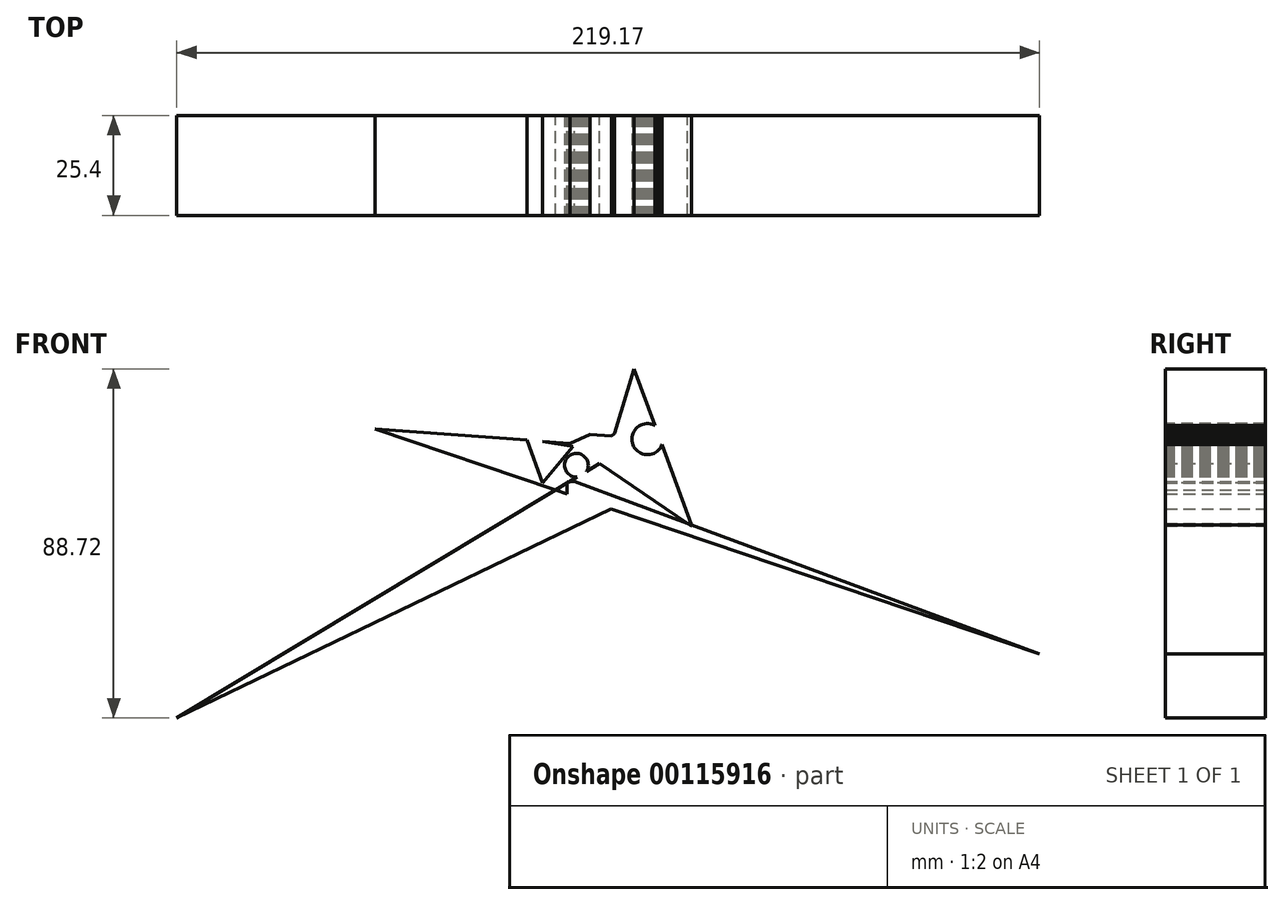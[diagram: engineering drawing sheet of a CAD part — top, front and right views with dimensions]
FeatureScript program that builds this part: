
annotation { "Feature Type Name" : "Feature", "Feature Type Description" : "" }
export const myFeature = defineFeature(function(context is Context, id is Id, definition is map)
    precondition{}
    {
        {
            var Q0;
            Q0=qCreatedBy(makeId("Front.planeOp"),FACE);
            var sketch = newSketch(context, id + "F0", { "sketchPlane" : qUnion([Q0])});
            skLineSegment(sketch, "E0", {"start": v(0.1, 0.1) * mm, "end": v(0.1, 31.83) * mm});
            skLineSegment(sketch, "E1", {"start": v(0.1, 31.24) * mm, "end": v(6.37, 32.02) * mm});
            skLineSegment(sketch, "E2", {"start": v(6.37, 32.02) * mm, "end": v(22.82, 30.06) * mm});
            skLineSegment(sketch, "E3", {"start": v(23.01, 30.06) * mm, "end": v(-99, -28.7) * mm});
            skLineSegment(sketch, "E4", {"start": v(-99, -28.7) * mm, "end": v(8.32, 35.94) * mm});
            skLineSegment(sketch, "E5", {"start": v(8.32, 35.94) * mm, "end": v(31.83, 20.08) * mm});
            skLineSegment(sketch, "E6", {"start": v(31.83, 20.08) * mm, "end": v(17.14, 60.03) * mm});
            skLineSegment(sketch, "E7", {"start": v(17.14, 60.03) * mm, "end": v(12.24, 43.58) * mm});
            skLineSegment(sketch, "E8", {"start": v(12.24, 43.58) * mm, "end": v(11.46, 43) * mm});
            skLineSegment(sketch, "E9", {"start": v(11.46, 43) * mm, "end": v(5.97, 43.38) * mm});
            skLineSegment(sketch, "E10", {"start": v(5.97, 43.38) * mm, "end": v(-17.92, 38.88) * mm});
            skLineSegment(sketch, "E11", {"start": v(-17.92, 38.88) * mm, "end": v(120.16, -12.44) * mm});
            skLineSegment(sketch, "E12", {"start": v(120.16, -12.44) * mm, "end": v(-48.67, 44.75) * mm});
            skLineSegment(sketch, "E13", {"start": v(-48.67, 44.75) * mm, "end": v(0.88, 41.13) * mm});
            skPoint(sketch, "E13.endSnap0", {"position": v(-5.97, 41.13) * mm});
            skLineSegment(sketch, "E14", {"start": v(0.88, 41.13) * mm, "end": v(5.97, 43.38) * mm});
            skSolve(sketch);
        }
        {
            var Q0;
            {var subQ1=sQuery(id+"F0.wireOp",EDGE,"E0");var subQ5=sQuery(id+"F0.wireOp",EDGE,"E12");var subQ10=makeQuery(id+"F0.imprint","INTERSECT",VERTEX,{"derivedFrom":[subQ1,subQ5]});Q0=makeQuery(id+"F0.imprint","IMPRINT",FACE,{"disambiguationData":[TD([[makeQuery(id+"F0.imprint","IMPRINT",EDGE,{"disambiguationData":[TD([[subQ10,-1.0]])],"derivedFrom":subQ1}),-1.0]])]});}
            var Q1;
            {var subQ8=sQuery(id+"F0.wireOp",EDGE,"E7");Q1=makeQuery(id+"F0.imprint","IMPRINT",FACE,{"disambiguationData":[TD([[makeQuery(id+"F0.imprint","IMPRINT",EDGE,{"derivedFrom":subQ8}),1.0]])]});}
            var Q2;
            {var subQ0=sQuery(id+"F0.wireOp",EDGE,"E3");var subQ1=sQuery(id+"F0.wireOp",EDGE,"E0");var subQ2=makeQuery(id+"F0.imprint","INTERSECT",VERTEX,{"derivedFrom":[subQ1,subQ0]});Q2=makeQuery(id+"F0.imprint","IMPRINT",FACE,{"disambiguationData":[TD([[makeQuery(id+"F0.imprint","IMPRINT",EDGE,{"disambiguationData":[TD([[subQ2,-1.0]])],"derivedFrom":subQ1}),-1.0]])]});}
            var Q3;
            {var subQ1=sQuery(id+"F0.wireOp",EDGE,"E1");var subQ7=sQuery(id+"F0.wireOp",EDGE,"E0");var subQ11=makeQuery(id+"F0.imprint","INTERSECT",VERTEX,{"derivedFrom":[subQ7,subQ1]});Q3=makeQuery(id+"F0.imprint","IMPRINT",FACE,{"disambiguationData":[TD([[makeQuery(id+"F0.imprint","IMPRINT",EDGE,{"disambiguationData":[TD([[subQ11,1.0]])],"derivedFrom":subQ7}),1.0]])]});}
            var Q4;
            {var subQ1=sQuery(id+"F0.wireOp",EDGE,"E3");var subQ8=sQuery(id+"F0.wireOp",EDGE,"E12");var subQ9=makeQuery(id+"F0.imprint","INTERSECT",VERTEX,{"derivedFrom":[subQ1,subQ8]});Q4=makeQuery(id+"F0.imprint","IMPRINT",FACE,{"disambiguationData":[TD([[makeQuery(id+"F0.imprint","IMPRINT",EDGE,{"disambiguationData":[TD([[subQ9,1.0]])],"derivedFrom":subQ1}),1.0]])]});}
            var Q5;
            {var subQ0=sQuery(id+"F0.wireOp",EDGE,"E3");var subQ1=sQuery(id+"F0.wireOp",EDGE,"E0");var subQ2=makeQuery(id+"F0.imprint","INTERSECT",VERTEX,{"derivedFrom":[subQ1,subQ0]});Q5=makeQuery(id+"F0.imprint","IMPRINT",FACE,{"disambiguationData":[TD([[makeQuery(id+"F0.imprint","IMPRINT",EDGE,{"disambiguationData":[TD([[subQ2,-1.0]])],"derivedFrom":subQ1}),1.0]])]});}
            extrude(context, id + "F1", {"entities" : qUnion([Q0, Q1, Q2, Q3, Q4, Q5]), "depth" : 25.4 * mm});
        }
        {
            var Q0;
            Q0=makeQuery(id+"F1.opExtrude","CAP_FACE",FACE,{"disambiguationData":[OSD([sQuery(id+"F0.wireOp",EDGE,"E0"),sQuery(id+"F0.wireOp",EDGE,"E1"),sQuery(id+"F0.wireOp",EDGE,"E4"),sQuery(id+"F0.wireOp",EDGE,"E5"),sQuery(id+"F0.wireOp",EDGE,"E6"),sQuery(id+"F0.wireOp",EDGE,"E7"),sQuery(id+"F0.wireOp",EDGE,"E8"),sQuery(id+"F0.wireOp",EDGE,"E9"),sQuery(id+"F0.wireOp",EDGE,"E11"),sQuery(id+"F0.wireOp",EDGE,"E12"),sQuery(id+"F0.wireOp",EDGE,"E13"),sQuery(id+"F0.wireOp",EDGE,"E14")])],"isStart":false});
            var sketch = newSketch(context, id + "F2", { "sketchPlane" : qUnion([Q0])});
            skCircle(sketch, "E15.cCircle", {"center": v(-4.88, 37.91) * mm, "radius": 3.46 * mm, "construction": true});
            skLineSegment(sketch, "E15.0", {"start": v(-6.06, 31.09) * mm, "end": v(-10.2, 42.35) * mm});
            skLineSegment(sketch, "E15.1", {"start": v(-10.2, 42.35) * mm, "end": v(1.62, 40.3) * mm});
            skLineSegment(sketch, "E15.2", {"start": v(1.62, 40.3) * mm, "end": v(-6.06, 31.09) * mm});
            skPoint(sketch, "E15.0.midPoint", {"position": v(-8.13, 36.72) * mm});
            skCircle(sketch, "E16.cCircle", {"center": v(2.51, 35.56) * mm, "radius": 3.01 * mm, "construction": true});
            skLineSegment(sketch, "E16.0", {"start": v(4.76, 37.58) * mm, "end": v(5, 37.28) * mm});
            skLineSegment(sketch, "E16.1", {"start": v(5, 37.28) * mm, "end": v(5.19, 36.95) * mm});
            skLineSegment(sketch, "E16.2", {"start": v(5.19, 36.95) * mm, "end": v(5.34, 36.6) * mm});
            skLineSegment(sketch, "E16.3", {"start": v(5.34, 36.6) * mm, "end": v(5.45, 36.24) * mm});
            skLineSegment(sketch, "E16.4", {"start": v(5.45, 36.24) * mm, "end": v(5.51, 35.87) * mm});
            skLineSegment(sketch, "E16.5", {"start": v(5.51, 35.87) * mm, "end": v(5.53, 35.5) * mm});
            skLineSegment(sketch, "E16.6", {"start": v(5.53, 35.5) * mm, "end": v(5.5, 35.11) * mm});
            skLineSegment(sketch, "E16.7", {"start": v(5.5, 35.11) * mm, "end": v(5.42, 34.74) * mm});
            skLineSegment(sketch, "E16.8", {"start": v(5.42, 34.74) * mm, "end": v(5.3, 34.39) * mm});
            skLineSegment(sketch, "E16.9", {"start": v(5.3, 34.39) * mm, "end": v(5.12, 34.05) * mm});
            skLineSegment(sketch, "E16.10", {"start": v(5.12, 34.05) * mm, "end": v(4.91, 33.73) * mm});
            skLineSegment(sketch, "E16.11", {"start": v(4.91, 33.73) * mm, "end": v(4.66, 33.45) * mm});
            skLineSegment(sketch, "E16.12", {"start": v(4.66, 33.45) * mm, "end": v(4.38, 33.2) * mm});
            skLineSegment(sketch, "E16.13", {"start": v(4.38, 33.2) * mm, "end": v(4.07, 32.98) * mm});
            skLineSegment(sketch, "E16.14", {"start": v(4.07, 32.98) * mm, "end": v(3.73, 32.8) * mm});
            skLineSegment(sketch, "E16.15", {"start": v(3.73, 32.8) * mm, "end": v(3.38, 32.67) * mm});
            skLineSegment(sketch, "E16.16", {"start": v(3.38, 32.67) * mm, "end": v(3, 32.59) * mm});
            skLineSegment(sketch, "E16.17", {"start": v(3, 32.59) * mm, "end": v(2.63, 32.55) * mm});
            skLineSegment(sketch, "E16.18", {"start": v(2.63, 32.55) * mm, "end": v(2.25, 32.56) * mm});
            skLineSegment(sketch, "E16.19", {"start": v(2.25, 32.56) * mm, "end": v(1.88, 32.61) * mm});
            skLineSegment(sketch, "E16.20", {"start": v(1.88, 32.61) * mm, "end": v(1.51, 32.71) * mm});
            skLineSegment(sketch, "E16.21", {"start": v(1.51, 32.71) * mm, "end": v(1.16, 32.86) * mm});
            skLineSegment(sketch, "E16.22", {"start": v(1.16, 32.86) * mm, "end": v(0.84, 33.05) * mm});
            skLineSegment(sketch, "E16.23", {"start": v(0.84, 33.05) * mm, "end": v(0.54, 33.28) * mm});
            skLineSegment(sketch, "E16.24", {"start": v(0.54, 33.28) * mm, "end": v(0.27, 33.55) * mm});
            skLineSegment(sketch, "E16.25", {"start": v(0.27, 33.55) * mm, "end": v(0.03, 33.84) * mm});
            skLineSegment(sketch, "E16.26", {"start": v(0.03, 33.84) * mm, "end": v(-0.17, 34.17) * mm});
            skLineSegment(sketch, "E16.27", {"start": v(-0.17, 34.17) * mm, "end": v(-0.32, 34.52) * mm});
            skLineSegment(sketch, "E16.28", {"start": v(-0.32, 34.52) * mm, "end": v(-0.43, 34.88) * mm});
            skLineSegment(sketch, "E16.29", {"start": v(-0.43, 34.88) * mm, "end": v(-0.49, 35.25) * mm});
            skLineSegment(sketch, "E16.30", {"start": v(-0.49, 35.25) * mm, "end": v(-0.5, 35.63) * mm});
            skLineSegment(sketch, "E16.31", {"start": v(-0.5, 35.63) * mm, "end": v(-0.47, 36) * mm});
            skLineSegment(sketch, "E16.32", {"start": v(-0.47, 36) * mm, "end": v(-0.4, 36.38) * mm});
            skLineSegment(sketch, "E16.33", {"start": v(-0.4, 36.38) * mm, "end": v(-0.27, 36.74) * mm});
            skLineSegment(sketch, "E16.34", {"start": v(-0.27, 36.74) * mm, "end": v(-0.1, 37.08) * mm});
            skLineSegment(sketch, "E16.35", {"start": v(-0.1, 37.08) * mm, "end": v(0.11, 37.4) * mm});
            skLineSegment(sketch, "E16.36", {"start": v(0.11, 37.4) * mm, "end": v(0.36, 37.68) * mm});
            skLineSegment(sketch, "E16.37", {"start": v(0.36, 37.68) * mm, "end": v(0.64, 37.93) * mm});
            skLineSegment(sketch, "E16.38", {"start": v(0.64, 37.93) * mm, "end": v(0.95, 38.15) * mm});
            skLineSegment(sketch, "E16.39", {"start": v(0.95, 38.15) * mm, "end": v(1.3, 38.32) * mm});
            skLineSegment(sketch, "E16.40", {"start": v(1.3, 38.32) * mm, "end": v(1.65, 38.45) * mm});
            skLineSegment(sketch, "E16.41", {"start": v(1.65, 38.45) * mm, "end": v(2.01, 38.54) * mm});
            skLineSegment(sketch, "E16.42", {"start": v(2.01, 38.54) * mm, "end": v(2.4, 38.58) * mm});
            skLineSegment(sketch, "E16.43", {"start": v(2.4, 38.58) * mm, "end": v(2.77, 38.57) * mm});
            skLineSegment(sketch, "E16.44", {"start": v(2.77, 38.57) * mm, "end": v(3.15, 38.51) * mm});
            skLineSegment(sketch, "E16.45", {"start": v(3.15, 38.51) * mm, "end": v(3.5, 38.4) * mm});
            skLineSegment(sketch, "E16.46", {"start": v(3.5, 38.4) * mm, "end": v(3.86, 38.26) * mm});
            skLineSegment(sketch, "E16.47", {"start": v(3.86, 38.26) * mm, "end": v(4.19, 38.07) * mm});
            skLineSegment(sketch, "E16.48", {"start": v(4.19, 38.07) * mm, "end": v(4.49, 37.84) * mm});
            skLineSegment(sketch, "E16.49", {"start": v(4.49, 37.84) * mm, "end": v(4.76, 37.58) * mm});
            skPoint(sketch, "E16.0.midPoint", {"position": v(4.88, 37.43) * mm});
            skCircle(sketch, "E17.cCircle", {"center": v(20.53, 42.17) * mm, "radius": 3.94 * mm, "construction": true});
            skLineSegment(sketch, "E17.0", {"start": v(17.32, 39.88) * mm, "end": v(17.06, 40.3) * mm});
            skLineSegment(sketch, "E17.1", {"start": v(17.06, 40.3) * mm, "end": v(16.85, 40.75) * mm});
            skLineSegment(sketch, "E17.2", {"start": v(16.85, 40.75) * mm, "end": v(16.7, 41.22) * mm});
            skLineSegment(sketch, "E17.3", {"start": v(16.7, 41.22) * mm, "end": v(16.61, 41.71) * mm});
            skLineSegment(sketch, "E17.4", {"start": v(16.61, 41.71) * mm, "end": v(16.59, 42.2) * mm});
            skLineSegment(sketch, "E17.5", {"start": v(16.59, 42.2) * mm, "end": v(16.62, 42.7) * mm});
            skLineSegment(sketch, "E17.6", {"start": v(16.62, 42.7) * mm, "end": v(16.72, 43.19) * mm});
            skLineSegment(sketch, "E17.7", {"start": v(16.72, 43.19) * mm, "end": v(16.87, 43.66) * mm});
            skLineSegment(sketch, "E17.8", {"start": v(16.87, 43.66) * mm, "end": v(17.09, 44.1) * mm});
            skLineSegment(sketch, "E17.9", {"start": v(17.09, 44.1) * mm, "end": v(17.36, 44.52) * mm});
            skLineSegment(sketch, "E17.10", {"start": v(17.36, 44.52) * mm, "end": v(17.68, 44.9) * mm});
            skLineSegment(sketch, "E17.11", {"start": v(17.68, 44.9) * mm, "end": v(18.04, 45.23) * mm});
            skLineSegment(sketch, "E17.12", {"start": v(18.04, 45.23) * mm, "end": v(18.44, 45.52) * mm});
            skLineSegment(sketch, "E17.13", {"start": v(18.44, 45.52) * mm, "end": v(18.88, 45.75) * mm});
            skLineSegment(sketch, "E17.14", {"start": v(18.88, 45.75) * mm, "end": v(19.34, 45.93) * mm});
            skLineSegment(sketch, "E17.15", {"start": v(19.34, 45.93) * mm, "end": v(19.82, 46.05) * mm});
            skLineSegment(sketch, "E17.16", {"start": v(19.82, 46.05) * mm, "end": v(20.32, 46.1) * mm});
            skLineSegment(sketch, "E17.17", {"start": v(20.32, 46.1) * mm, "end": v(20.81, 46.1) * mm});
            skLineSegment(sketch, "E17.18", {"start": v(20.81, 46.1) * mm, "end": v(21.3, 46.04) * mm});
            skLineSegment(sketch, "E17.19", {"start": v(21.3, 46.04) * mm, "end": v(21.78, 45.91) * mm});
            skLineSegment(sketch, "E17.20", {"start": v(21.78, 45.91) * mm, "end": v(22.24, 45.73) * mm});
            skLineSegment(sketch, "E17.21", {"start": v(22.24, 45.73) * mm, "end": v(22.67, 45.48) * mm});
            skLineSegment(sketch, "E17.22", {"start": v(22.67, 45.48) * mm, "end": v(23.07, 45.19) * mm});
            skLineSegment(sketch, "E17.23", {"start": v(23.07, 45.19) * mm, "end": v(23.43, 44.85) * mm});
            skLineSegment(sketch, "E17.24", {"start": v(23.43, 44.85) * mm, "end": v(23.74, 44.46) * mm});
            skLineSegment(sketch, "E17.25", {"start": v(23.74, 44.46) * mm, "end": v(24, 44.04) * mm});
            skLineSegment(sketch, "E17.26", {"start": v(24, 44.04) * mm, "end": v(24.2, 43.6) * mm});
            skLineSegment(sketch, "E17.27", {"start": v(24.2, 43.6) * mm, "end": v(24.36, 43.12) * mm});
            skLineSegment(sketch, "E17.28", {"start": v(24.36, 43.12) * mm, "end": v(24.45, 42.63) * mm});
            skLineSegment(sketch, "E17.29", {"start": v(24.45, 42.63) * mm, "end": v(24.47, 42.14) * mm});
            skLineSegment(sketch, "E17.30", {"start": v(24.47, 42.14) * mm, "end": v(24.44, 41.64) * mm});
            skLineSegment(sketch, "E17.31", {"start": v(24.44, 41.64) * mm, "end": v(24.34, 41.16) * mm});
            skLineSegment(sketch, "E17.32", {"start": v(24.34, 41.16) * mm, "end": v(24.18, 40.69) * mm});
            skLineSegment(sketch, "E17.33", {"start": v(24.18, 40.69) * mm, "end": v(23.97, 40.24) * mm});
            skLineSegment(sketch, "E17.34", {"start": v(23.97, 40.24) * mm, "end": v(23.7, 39.83) * mm});
            skLineSegment(sketch, "E17.35", {"start": v(23.7, 39.83) * mm, "end": v(23.38, 39.45) * mm});
            skLineSegment(sketch, "E17.36", {"start": v(23.38, 39.45) * mm, "end": v(23.02, 39.11) * mm});
            skLineSegment(sketch, "E17.37", {"start": v(23.02, 39.11) * mm, "end": v(22.61, 38.82) * mm});
            skLineSegment(sketch, "E17.38", {"start": v(22.61, 38.82) * mm, "end": v(22.18, 38.59) * mm});
            skLineSegment(sketch, "E17.39", {"start": v(22.18, 38.59) * mm, "end": v(21.71, 38.41) * mm});
            skLineSegment(sketch, "E17.40", {"start": v(21.71, 38.41) * mm, "end": v(21.23, 38.3) * mm});
            skLineSegment(sketch, "E17.41", {"start": v(21.23, 38.3) * mm, "end": v(20.74, 38.23) * mm});
            skLineSegment(sketch, "E17.42", {"start": v(20.74, 38.23) * mm, "end": v(20.25, 38.24) * mm});
            skLineSegment(sketch, "E17.43", {"start": v(20.25, 38.24) * mm, "end": v(19.76, 38.3) * mm});
            skLineSegment(sketch, "E17.44", {"start": v(19.76, 38.3) * mm, "end": v(19.28, 38.43) * mm});
            skLineSegment(sketch, "E17.45", {"start": v(19.28, 38.43) * mm, "end": v(18.82, 38.62) * mm});
            skLineSegment(sketch, "E17.46", {"start": v(18.82, 38.62) * mm, "end": v(18.39, 38.86) * mm});
            skLineSegment(sketch, "E17.47", {"start": v(18.39, 38.86) * mm, "end": v(17.99, 39.16) * mm});
            skLineSegment(sketch, "E17.48", {"start": v(17.99, 39.16) * mm, "end": v(17.63, 39.5) * mm});
            skLineSegment(sketch, "E17.49", {"start": v(17.63, 39.5) * mm, "end": v(17.32, 39.88) * mm});
            skPoint(sketch, "E17.0.midPoint", {"position": v(17.19, 40.1) * mm});
            skSolve(sketch);
        }
        {
            var Q0;
            Q0=makeQuery(id+"F2.imprint","IMPRINT",FACE,{"disambiguationData":[TD([[makeQuery(id+"F2.imprint","IMPRINT",EDGE,{"derivedFrom":sQuery(id+"F2.wireOp",EDGE,"E16.0")}),-1.0]])]});
            var Q1;
            Q1=makeQuery(id+"F2.imprint","IMPRINT",FACE,{"disambiguationData":[TD([[makeQuery(id+"F2.imprint","IMPRINT",EDGE,{"derivedFrom":sQuery(id+"F2.wireOp",EDGE,"E17.0")}),-1.0]])]});
            var Q2;
            {var subQ0=sQuery(id+"F2.wireOp",EDGE,"E15.2");Q2=makeQuery(id+"F2.imprint","IMPRINT",FACE,{"disambiguationData":[TD([[makeQuery(id+"F2.imprint","IMPRINT",EDGE,{"derivedFrom":subQ0}),-1.0]])]});}
            extrude(context, id + "F3", {"entities" : qUnion([Q0, Q1, Q2]), "operationType" : NewBodyOperationType.REMOVE, "oppositeDirection" : true, "depth" : 25.4 * mm});
        }
    });
